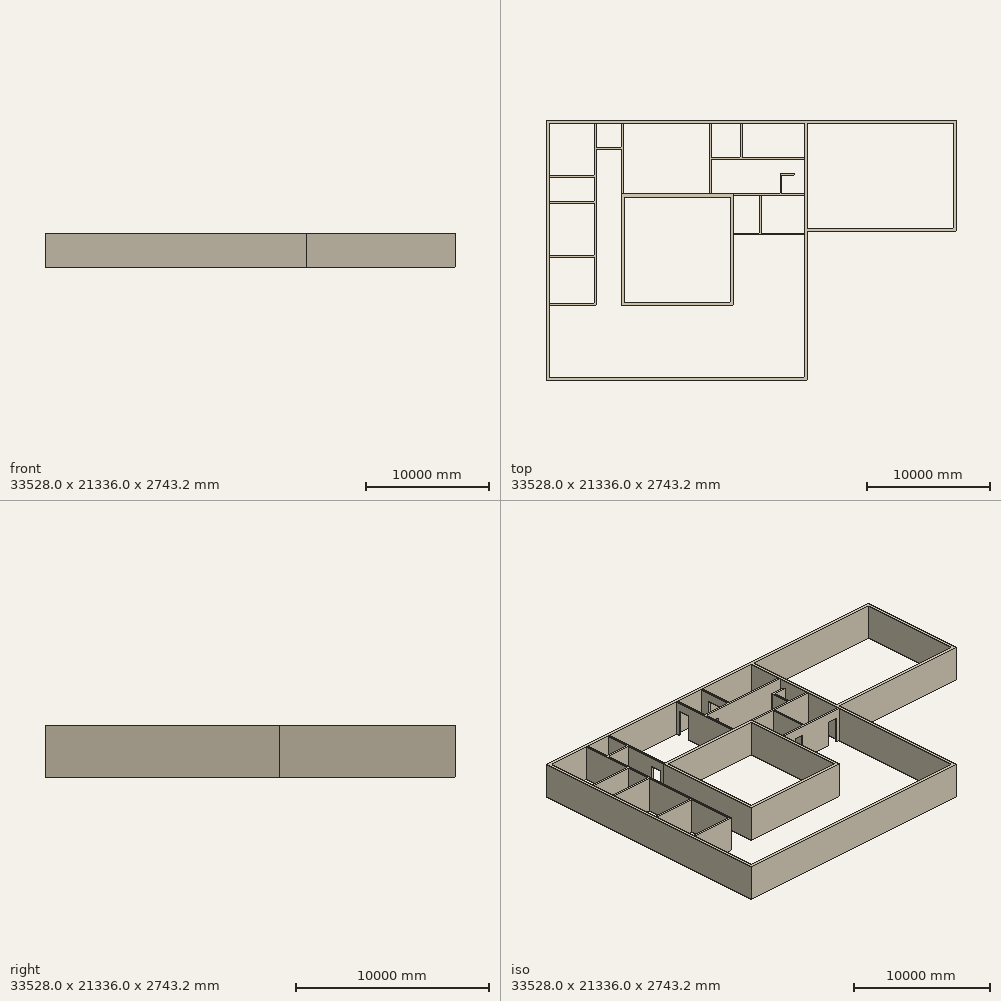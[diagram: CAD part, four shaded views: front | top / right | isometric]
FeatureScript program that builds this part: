
annotation { "Feature Type Name" : "Feature", "Feature Type Description" : "" }
export const myFeature = defineFeature(function(context is Context, id is Id, definition is map)
    precondition{}
    {
        {
            var Q0;
            Q0=qCreatedBy(makeId("Top.planeOp"),FACE);
            var sketch = newSketch(context, id + "F0", { "sketchPlane" : qUnion([Q0])});
            skLineSegment(sketch, "E0.bottom", {"start": v(0, 0) * mm, "end": v(21336, 0) * mm});
            skLineSegment(sketch, "E0.top", {"start": v(0, 21336) * mm, "end": v(33528, 21336) * mm});
            skLineSegment(sketch, "E0.left", {"start": v(0, 0) * mm, "end": v(0, 21336) * mm});
            skLineSegment(sketch, "E0.right", {"start": v(21336, 0) * mm, "end": v(21336, 21082) * mm});
            skLineSegment(sketch, "E1.0", {"start": v(254, 21082) * mm, "end": v(21082, 21082) * mm});
            skLineSegment(sketch, "E1.1", {"start": v(254, 254) * mm, "end": v(254, 21082) * mm});
            skLineSegment(sketch, "E1.2", {"start": v(254, 254) * mm, "end": v(21082, 254) * mm});
            skLineSegment(sketch, "E1.3", {"start": v(21082, 254) * mm, "end": v(21082, 21082) * mm});
            skLineSegment(sketch, "E2.left", {"start": v(33274, 21082) * mm, "end": v(33274, 12446) * mm});
            skLineSegment(sketch, "E2.right", {"start": v(33528, 21336) * mm, "end": v(33528, 12192) * mm});
            skLineSegment(sketch, "E3.bottom", {"start": v(21336, 12446) * mm, "end": v(33274, 12446) * mm});
            skLineSegment(sketch, "E3.top", {"start": v(21336, 12192) * mm, "end": v(33528, 12192) * mm});
            skLineSegment(sketch, "E3.left", {"start": v(21336, 12446) * mm, "end": v(21336, 12192) * mm});
            skLineSegment(sketch, "E4", {"start": v(21336, 21082) * mm, "end": v(33274, 21082) * mm});
            skSolve(sketch);
        }
        {
            var Q0;
            Q0=qSketchRegion(id+"F0",true);
            extrude(context, id + "F1", {"entities" : qUnion([Q0]), "depth" : 2743.2 * mm});
        }
        {
            var Q0;
            Q0=qCreatedBy(makeId("Top.planeOp"),FACE);
            var sketch = newSketch(context, id + "F2", { "sketchPlane" : qUnion([Q0])});
            skLineSegment(sketch, "E5.bottom", {"start": v(6146.8, 15290.8) * mm, "end": v(15290.8, 15290.8) * mm});
            skLineSegment(sketch, "E5.top", {"start": v(6146.8, 6146.8) * mm, "end": v(15290.8, 6146.8) * mm});
            skLineSegment(sketch, "E5.left", {"start": v(6146.8, 15290.8) * mm, "end": v(6146.8, 6146.8) * mm});
            skLineSegment(sketch, "E5.right", {"start": v(15290.8, 15290.8) * mm, "end": v(15290.8, 6146.8) * mm});
            skLineSegment(sketch, "E6.0", {"start": v(6400.8, 15036.8) * mm, "end": v(15036.8, 15036.8) * mm});
            skLineSegment(sketch, "E6.1", {"start": v(6400.8, 15036.8) * mm, "end": v(6400.8, 6400.8) * mm});
            skLineSegment(sketch, "E6.2", {"start": v(6400.8, 6400.8) * mm, "end": v(15036.8, 6400.8) * mm});
            skLineSegment(sketch, "E6.3", {"start": v(15036.8, 15036.8) * mm, "end": v(15036.8, 6400.8) * mm});
            skSolve(sketch);
        }
        {
            var Q0;
            Q0=qSketchRegion(id+"F2",true);
            extrude(context, id + "F3", {"entities" : qUnion([Q0]), "depth" : 2743.2 * mm});
        }
        {
            var Q0;
            Q0=qCreatedBy(makeId("Top.planeOp"),FACE);
            var sketch = newSketch(context, id + "F4", { "sketchPlane" : qUnion([Q0])});
            skLineSegment(sketch, "E7.bottom", {"start": v(15290.8, 15290.8) * mm, "end": v(21082, 15290.8) * mm});
            skLineSegment(sketch, "E7.top", {"start": v(15290.8, 15138.4) * mm, "end": v(21082, 15138.4) * mm});
            skLineSegment(sketch, "E7.left", {"start": v(15290.8, 15290.8) * mm, "end": v(15290.8, 15138.4) * mm});
            skLineSegment(sketch, "E7.right", {"start": v(21082, 15290.8) * mm, "end": v(21082, 15138.4) * mm});
            skLineSegment(sketch, "E8.bottom", {"start": v(19100.8, 15290.8) * mm, "end": v(19253.2, 15290.8) * mm});
            skLineSegment(sketch, "E8.left", {"start": v(19100.8, 15290.8) * mm, "end": v(19100.8, 16967.2) * mm});
            skLineSegment(sketch, "E8.right", {"start": v(19253.2, 15290.8) * mm, "end": v(19253.2, 16814.8) * mm});
            skLineSegment(sketch, "E9.bottom", {"start": v(19100.8, 16967.2) * mm, "end": v(20320, 16967.2) * mm});
            skLineSegment(sketch, "E9.right", {"start": v(20320, 16967.2) * mm, "end": v(20320, 16814.8) * mm});
            skLineSegment(sketch, "E10.trimOffspring", {"start": v(19253.2, 16814.8) * mm, "end": v(20320, 16814.8) * mm});
            skSolve(sketch);
        }
        {
            var Q0;
            Q0=qSketchRegion(id+"F4",true);
            extrude(context, id + "F5", {"entities" : qUnion([Q0]), "offsetDistance" : 25.4 * mm, "depth" : 2743.2 * mm});
        }
        {
            var Q0;
            Q0=qCreatedBy(makeId("Top.planeOp"),FACE);
            var sketch = newSketch(context, id + "F6", { "sketchPlane" : qUnion([Q0])});
            skLineSegment(sketch, "E11", {"start": v(13309.6, 21082) * mm, "end": v(13309.6, 15290.8) * mm});
            skLineSegment(sketch, "E12", {"start": v(13309.6, 15290.8) * mm, "end": v(13462, 15290.8) * mm});
            skLineSegment(sketch, "E13", {"start": v(13462, 15290.8) * mm, "end": v(13462, 18110.2) * mm});
            skLineSegment(sketch, "E14", {"start": v(13462, 18110.2) * mm, "end": v(21082, 18110.2) * mm});
            skLineSegment(sketch, "E15", {"start": v(21082, 18110.2) * mm, "end": v(21082, 18262.6) * mm});
            skLineSegment(sketch, "E16", {"start": v(21082, 18262.6) * mm, "end": v(16002, 18262.6) * mm});
            skLineSegment(sketch, "E17", {"start": v(13462, 18262.6) * mm, "end": v(13462, 21082) * mm});
            skLineSegment(sketch, "E18", {"start": v(13462, 21082) * mm, "end": v(13309.6, 21082) * mm});
            skLineSegment(sketch, "E19.bottom", {"start": v(15849.6, 21082) * mm, "end": v(16002, 21082) * mm});
            skLineSegment(sketch, "E19.left", {"start": v(15849.6, 21082) * mm, "end": v(15849.6, 18262.6) * mm});
            skLineSegment(sketch, "E19.right", {"start": v(16002, 21082) * mm, "end": v(16002, 18262.6) * mm});
            skLineSegment(sketch, "E20.trimOffspring", {"start": v(15849.6, 18262.6) * mm, "end": v(13462, 18262.6) * mm});
            skSolve(sketch);
        }
        {
            var Q0;
            Q0=qSketchRegion(id+"F6",true);
            extrude(context, id + "F7", {"entities" : qUnion([Q0]), "offsetDistance" : 25.4 * mm, "depth" : 2743.2 * mm});
        }
        {
            var Q0;
            Q0=qCreatedBy(makeId("Top.planeOp"),FACE);
            var sketch = newSketch(context, id + "F8", { "sketchPlane" : qUnion([Q0])});
            skLineSegment(sketch, "E21.bottom", {"start": v(6146.8, 21082) * mm, "end": v(6299.2, 21082) * mm});
            skLineSegment(sketch, "E21.top", {"start": v(6146.8, 15290.8) * mm, "end": v(6299.2, 15290.8) * mm});
            skLineSegment(sketch, "E21.left", {"start": v(6146.8, 21082) * mm, "end": v(6146.8, 15290.8) * mm});
            skLineSegment(sketch, "E21.right", {"start": v(6299.2, 21082) * mm, "end": v(6299.2, 15290.8) * mm});
            skSolve(sketch);
        }
        {
            var Q0;
            Q0=qSketchRegion(id+"F8",true);
            extrude(context, id + "F9", {"entities" : qUnion([Q0]), "offsetDistance" : 25.4 * mm, "depth" : 2743.2 * mm});
        }
        {
            var Q0;
            Q0=qCreatedBy(makeId("Top.planeOp"),FACE);
            var sketch = newSketch(context, id + "F10", { "sketchPlane" : qUnion([Q0])});
            skLineSegment(sketch, "E22.bottom", {"start": v(3911.6, 21081.97) * mm, "end": v(4064, 21081.97) * mm});
            skLineSegment(sketch, "E22.left", {"start": v(3911.6, 21081.97) * mm, "end": v(3911.6, 16814.8) * mm});
            skLineSegment(sketch, "E22.right", {"start": v(4064, 21081.97) * mm, "end": v(4064, 19100.8) * mm});
            skLineSegment(sketch, "E23.bottom", {"start": v(254.03, 16814.8) * mm, "end": v(3911.6, 16814.8) * mm});
            skLineSegment(sketch, "E23.top", {"start": v(254.03, 16662.4) * mm, "end": v(3911.6, 16662.4) * mm});
            skLineSegment(sketch, "E24.bottom", {"start": v(4064, 19100.8) * mm, "end": v(6146.8, 19100.8) * mm});
            skLineSegment(sketch, "E24.top", {"start": v(4064, 18948.4) * mm, "end": v(6146.8, 18948.4) * mm});
            skLineSegment(sketch, "E24.right", {"start": v(6146.8, 19100.8) * mm, "end": v(6146.8, 18948.4) * mm});
            skLineSegment(sketch, "E25.trimOffspring", {"start": v(4064, 18948.4) * mm, "end": v(4064, 6146.8) * mm});
            skLineSegment(sketch, "E26.bottom", {"start": v(254.03, 14681.2) * mm, "end": v(3911.6, 14681.2) * mm});
            skLineSegment(sketch, "E26.top", {"start": v(254.03, 14528.8) * mm, "end": v(3911.6, 14528.8) * mm});
            skLineSegment(sketch, "E27.trimOffspring", {"start": v(3911.6, 16662.4) * mm, "end": v(3911.6, 14681.2) * mm});
            skLineSegment(sketch, "E28.bottom", {"start": v(254.03, 10261.6) * mm, "end": v(3911.6, 10261.6) * mm});
            skLineSegment(sketch, "E28.top", {"start": v(254.03, 10109.2) * mm, "end": v(3911.6, 10109.2) * mm});
            skLineSegment(sketch, "E29.trimOffspring", {"start": v(3911.6, 14528.8) * mm, "end": v(3911.6, 10261.6) * mm});
            skLineSegment(sketch, "E30.bottom", {"start": v(254.03, 6299.2) * mm, "end": v(3911.6, 6299.2) * mm});
            skLineSegment(sketch, "E30.top", {"start": v(254.03, 6146.8) * mm, "end": v(4064, 6146.8) * mm});
            skLineSegment(sketch, "E31.trimOffspring", {"start": v(3911.6, 10109.2) * mm, "end": v(3911.6, 6299.2) * mm});
            skLineSegment(sketch, "E32", {"start": v(254.03, 6146.8) * mm, "end": v(254.03, 6299.2) * mm});
            skLineSegment(sketch, "E33", {"start": v(254.03, 10109.2) * mm, "end": v(254.03, 10261.6) * mm});
            skLineSegment(sketch, "E34", {"start": v(254.03, 14681.2) * mm, "end": v(254.03, 14528.8) * mm});
            skLineSegment(sketch, "E35", {"start": v(254.03, 16814.8) * mm, "end": v(254.03, 16662.4) * mm});
            skSolve(sketch);
        }
        {
            var Q0;
            Q0=qSketchRegion(id+"F10",true);
            extrude(context, id + "F11", {"entities" : qUnion([Q0]), "operationType" : NewBodyOperationType.ADD, "offsetDistance" : 25.4 * mm, "depth" : 2743.2 * mm});
        }
        {
            var Q0;
            Q0=qCreatedBy(makeId("Top.planeOp"),FACE);
            var sketch = newSketch(context, id + "F12", { "sketchPlane" : qUnion([Q0])});
            skLineSegment(sketch, "E36.bottom", {"start": v(17424.4, 15138.4) * mm, "end": v(17576.8, 15138.4) * mm});
            skLineSegment(sketch, "E36.left", {"start": v(17424.4, 15138.4) * mm, "end": v(17424.4, 12090.4) * mm});
            skLineSegment(sketch, "E36.right", {"start": v(17576.8, 15138.4) * mm, "end": v(17576.8, 12090.4) * mm});
            skLineSegment(sketch, "E37.bottom", {"start": v(15290.8, 12090.4) * mm, "end": v(17424.4, 12090.4) * mm});
            skLineSegment(sketch, "E37.top", {"start": v(15290.8, 11938) * mm, "end": v(21082, 11938) * mm});
            skLineSegment(sketch, "E37.left", {"start": v(15290.8, 12090.4) * mm, "end": v(15290.8, 11938) * mm});
            skLineSegment(sketch, "E38", {"start": v(17576.8, 12090.4) * mm, "end": v(21082, 12090.4) * mm});
            skLineSegment(sketch, "E39", {"start": v(21082, 12090.4) * mm, "end": v(21082, 11938) * mm});
            skSolve(sketch);
        }
        {
            var Q0;
            Q0=qSketchRegion(id+"F12",true);
            extrude(context, id + "F13", {"entities" : qUnion([Q0]), "offsetDistance" : 25.4 * mm, "depth" : 2743.2 * mm});
        }
        {
            var Q0;
            Q0=makeQuery(id+"F13.opExtrude","SWEPT_FACE",FACE,{"disambiguationData":[OSD([sQuery(id+"F12.wireOp",EDGE,"E37.top")])]});
            var sketch = newSketch(context, id + "F14", { "sketchPlane" : qUnion([Q0])});
            skLineSegment(sketch, "E40.bottom", {"start": v(16560.8, 0) * mm, "end": v(17272, 0) * mm});
            skLineSegment(sketch, "E40.top", {"start": v(16560.8, 2032) * mm, "end": v(17272, 2032) * mm});
            skLineSegment(sketch, "E40.left", {"start": v(16560.8, 0) * mm, "end": v(16560.8, 2032) * mm});
            skLineSegment(sketch, "E40.right", {"start": v(17272, 0) * mm, "end": v(17272, 2032) * mm});
            skLineSegment(sketch, "E41.bottom", {"start": v(19913.6, 0) * mm, "end": v(20828, 0) * mm});
            skLineSegment(sketch, "E41.top", {"start": v(19913.6, 2032) * mm, "end": v(20828, 2032) * mm});
            skLineSegment(sketch, "E41.left", {"start": v(19913.6, 0) * mm, "end": v(19913.6, 2032) * mm});
            skLineSegment(sketch, "E41.right", {"start": v(20828, 0) * mm, "end": v(20828, 2032) * mm});
            skSolve(sketch);
        }
        {
            var Q0;
            Q0=qSketchRegion(id+"F14",true);
            extrude(context, id + "F15", {"entities" : qUnion([Q0]), "operationType" : NewBodyOperationType.REMOVE, "oppositeDirection" : true, "depth" : 152.4 * mm});
        }
        {
            var Q0;
            Q0=makeQuery(id+"F7.opExtrude","SWEPT_FACE",FACE,{"disambiguationData":[OSD([sQuery(id+"F6.wireOp",EDGE,"E20.trimOffspring")])]});
            var sketch = newSketch(context, id + "F16", { "sketchPlane" : qUnion([Q0])});
            skLineSegment(sketch, "E42.bottom", {"start": v(-14630.4, 0) * mm, "end": v(-13716, 0) * mm});
            skLineSegment(sketch, "E42.top", {"start": v(-14630.4, 2032) * mm, "end": v(-13716, 2032) * mm});
            skLineSegment(sketch, "E42.left", {"start": v(-14630.4, 0) * mm, "end": v(-14630.4, 2032) * mm});
            skLineSegment(sketch, "E42.right", {"start": v(-13716, 0) * mm, "end": v(-13716, 2032) * mm});
            skSolve(sketch);
        }
        {
            var Q0;
            Q0=qSketchRegion(id+"F16",true);
            extrude(context, id + "F17", {"entities" : qUnion([Q0]), "operationType" : NewBodyOperationType.REMOVE, "oppositeDirection" : true, "depth" : 152.4 * mm});
        }
        {
            var Q0;
            Q0=makeQuery(id+"F7.opExtrude","SWEPT_FACE",FACE,{"disambiguationData":[OSD([sQuery(id+"F6.wireOp",EDGE,"E19.right")])]});
            var sketch = newSketch(context, id + "F18", { "sketchPlane" : qUnion([Q0])});
            skLineSegment(sketch, "E43.bottom", {"start": v(19062.7, 0) * mm, "end": v(20281.9, 0) * mm});
            skLineSegment(sketch, "E43.top", {"start": v(19062.7, 2032) * mm, "end": v(20281.9, 2032) * mm});
            skLineSegment(sketch, "E43.left", {"start": v(19062.7, 0) * mm, "end": v(19062.7, 2032) * mm});
            skLineSegment(sketch, "E43.right", {"start": v(20281.9, 0) * mm, "end": v(20281.9, 2032) * mm});
            skSolve(sketch);
        }
        {
            var Q0;
            Q0=qSketchRegion(id+"F18",true);
            extrude(context, id + "F19", {"entities" : qUnion([Q0]), "operationType" : NewBodyOperationType.REMOVE, "oppositeDirection" : true, "depth" : 152.4 * mm});
        }
        {
            var Q0;
            Q0=makeQuery(id+"F7.opExtrude","SWEPT_FACE",FACE,{"disambiguationData":[OSD([sQuery(id+"F6.wireOp",EDGE,"E17")])]});
            var sketch = newSketch(context, id + "F20", { "sketchPlane" : qUnion([Q0])});
            skLineSegment(sketch, "E44.bottom", {"start": v(19913.6, 0) * mm, "end": v(20828, 0) * mm});
            skLineSegment(sketch, "E44.top", {"start": v(19913.6, 2032) * mm, "end": v(20828, 2032) * mm});
            skLineSegment(sketch, "E44.left", {"start": v(19913.6, 0) * mm, "end": v(19913.6, 2032) * mm});
            skLineSegment(sketch, "E44.right", {"start": v(20828, 0) * mm, "end": v(20828, 2032) * mm});
            skSolve(sketch);
        }
        {
            var Q0;
            Q0=qSketchRegion(id+"F20",true);
            extrude(context, id + "F21", {"entities" : qUnion([Q0]), "operationType" : NewBodyOperationType.REMOVE, "oppositeDirection" : true, "depth" : 152.4 * mm});
        }
        {
            var Q0;
            Q0=makeQuery(id+"F9.opExtrude","SWEPT_FACE",FACE,{"disambiguationData":[OSD([sQuery(id+"F8.wireOp",EDGE,"E21.left")])]});
            var sketch = newSketch(context, id + "F22", { "sketchPlane" : qUnion([Q0])});
            skLineSegment(sketch, "E45.bottom", {"start": v(-16510, 0) * mm, "end": v(-15595.6, 0) * mm});
            skLineSegment(sketch, "E45.top", {"start": v(-16510, 2032) * mm, "end": v(-15595.6, 2032) * mm});
            skLineSegment(sketch, "E45.left", {"start": v(-16510, 0) * mm, "end": v(-16510, 2032) * mm});
            skLineSegment(sketch, "E45.right", {"start": v(-15595.6, 0) * mm, "end": v(-15595.6, 2032) * mm});
            skSolve(sketch);
        }
        {
            var Q0;
            Q0=qSketchRegion(id+"F22",true);
            extrude(context, id + "F23", {"entities" : qUnion([Q0]), "operationType" : NewBodyOperationType.REMOVE, "oppositeDirection" : true, "depth" : 152.4 * mm});
        }
    });
